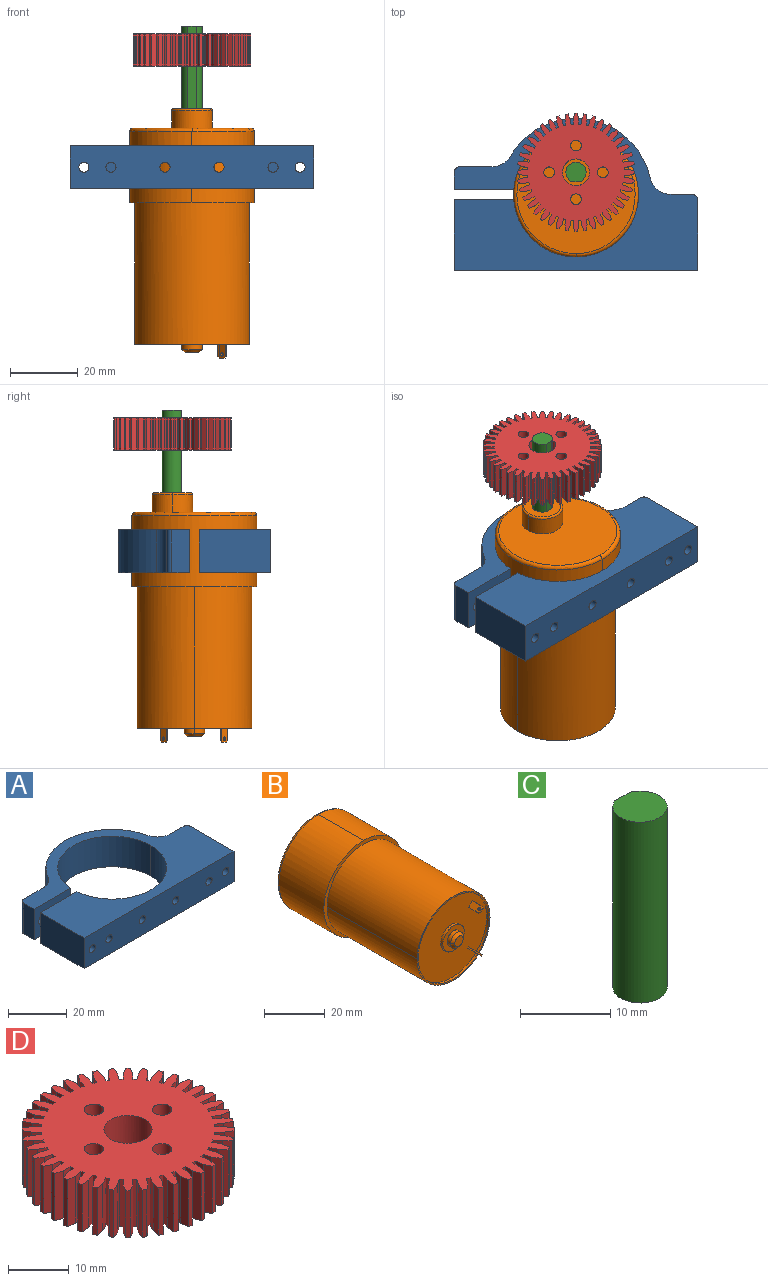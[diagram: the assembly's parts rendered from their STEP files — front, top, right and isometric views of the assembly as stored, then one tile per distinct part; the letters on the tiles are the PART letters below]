
ASSEMBLY  parts=4 mates=3
PART A: 26 faces, bbox 72x45.2x12.7 mm
  f0: cylinder r=1.85mm len=6.7mm, axis (0,-1,0), area 77.9mm2, adj f6,f9
  f1: plane 3.03x3.03mm, normal (0,-1,0), area 7.1mm2, adj f14
  f2: cylinder r=1.5mm len=12.7mm, axis (0,0,-1), area 29.9mm2, adj f12,f17,f18,f19
  f3: cylinder r=6.35mm len=12.7mm, axis (0,0,1), area 108.8mm2, adj f4,f12,f17,f19
  f4: cylinder r=22.5mm len=41.38mm, axis (0,0,1), area 683.2mm2, adj f3,f5,f17,f19
  f5: cylinder r=6.35mm len=12.7mm, axis (0,0,1), area 84mm2, adj f4,f6,f17,f19
  f6: plane 12.7x9.59mm, normal (0,1,0), area 111mm2, adj f0,f5,f7,f17,f19
  f7: cylinder r=1.5mm len=12.7mm, axis (0,0,-1), area 29.9mm2, adj f6,f8,f17,f19
  f8: plane 12.7x5.2mm, normal (-1,0,0), area 66mm2, adj f7,f9,f17,f19
  f9: plane 17.56x12.7mm, normal (0,-1,0), area 212.3mm2, adj f0,f8,f10,f17,f19
  f10: cylinder r=18.5mm len=36.94mm, axis (0,0,1), area 719mm2, adj f9,f11,f17,f19
  f11: cylinder r=18.5mm len=36.94mm, axis (0,0,1), area 702.8mm2, adj f10,f13,f15,f16,f17,f19
  f12: plane 12.7x6.36mm, normal (0,1,0), area 73.7mm2, adj f2,f3,f17,f19,f21
  f13: plane 17.56x12.7mm, normal (0,1,0), area 216mm2, adj f11,f17,f19,f20,f22
  f14: cylinder r=1.5mm len=20mm, axis (0,1,0), area 188.5mm2, adj f1,f24
  f15: cylinder r=1.5mm len=6.63mm, axis (0,1,0), area 58.6mm2, adj f11,f24
  f16: cylinder r=1.5mm len=5.82mm, axis (0,1,0), area 51.8mm2, adj f11,f24
  f17: plane 72x45.23mm, normal (0,0,-1), area 1409.8mm2, adj f2,f3,f4,f5,f6,f7,f8,f9
  f18: plane 21x12.7mm, normal (1,0,0), area 266.7mm2, adj f2,f17,f19,f24
  f19: plane 72x45.23mm, normal (0,0,1), area 1409.8mm2, adj f2,f3,f4,f5,f6,f7,f8,f9
  f20: plane 21x12.7mm, normal (-1,0,0), area 266.7mm2, adj f13,f17,f19,f24
  f21: cylinder r=1.5mm len=22.5mm, axis (0,-1,0), area 212.1mm2, adj f12,f24
  f22: cylinder r=1.5mm len=21mm, axis (0,-1,0), area 197.9mm2, adj f13,f24
  f23: plane 3.03x3.03mm, normal (0,-1,0), area 7.1mm2, adj f25
  f24: plane 72x12.7mm, normal (0,-1,0), area 872mm2, adj f14,f15,f16,f17,f18,f19,f20,f21
  f25: cylinder r=1.5mm len=20mm, axis (0,1,0), area 188.5mm2, adj f23,f24
PART B: 43 faces, bbox 40x73.8x40 mm
  f0: plane 4.02x4mm, normal (0,-1,0), area 12.6mm2, adj f1,f2
  f1: cone r=0mm half-angle=45deg, axis (0,1,0), area 11.1mm2, adj f0,f2,f3
  f2: cone r=0mm half-angle=45deg, axis (0,1,0), area 11.1mm2, adj f0,f1,f4
  f3: cylinder r=3mm len=6mm, axis (0,-1,0), area 14.1mm2, adj f1,f4,f6
  f4: cylinder r=3mm len=6mm, axis (0,-1,0), area 14.1mm2, adj f2,f3,f6
  f5: plane 11.02x11mm, normal (0,1,0), area 95mm2, adj f17,f18
  f6: plane 10.02x10mm, normal (0,-1,0), area 50.3mm2, adj f3,f4,f19,f20
  f7: plane 0.71x0.71mm, normal (-0.5,-0.71,0.5), area 0.4mm2, adj f8,f22,f23,f24
  f8: plane 1.41x1.41mm, normal (0,-1,0), area 0.8mm2, adj f7,f9,f22,f24
  f9: plane 0.71x0.71mm, normal (0.5,-0.71,-0.5), area 0.4mm2, adj f8,f21,f22,f24
  f10: cylinder r=0.5mm len=1.06mm, axis (-0.71,0,-0.71), area 0.8mm2, adj f11,f22,f24
  f11: cylinder r=0.5mm len=1.06mm, axis (-0.71,0,-0.71), area 0.8mm2, adj f10,f22,f24
  f12: plane 1.41x1.41mm, normal (0,-1,0), area 0.8mm2, adj f13,f14,f26,f28
  f13: plane 0.71x0.71mm, normal (0.5,-0.71,0.5), area 0.4mm2, adj f12,f25,f26,f28
  f14: plane 0.71x0.71mm, normal (-0.5,-0.71,-0.5), area 0.4mm2, adj f12,f26,f27,f28
  f15: cylinder r=0.5mm len=1.06mm, axis (-0.71,0,0.71), area 0.8mm2, adj f16,f26,f28
  f16: cylinder r=0.5mm len=1.06mm, axis (-0.71,0,0.71), area 0.8mm2, adj f15,f26,f28
  f17: torus R=5.5mm, axis (0,1,0), area 14.4mm2, adj f5,f18,f29
  f18: torus R=5.5mm, axis (0,1,0), area 14.4mm2, adj f5,f17,f30
  f19: cylinder r=5mm len=10mm, axis (0,-1,0), area 15.7mm2, adj f6,f20,f31
  f20: cylinder r=5mm len=10mm, axis (0,-1,0), area 15.7mm2, adj f6,f19,f31
  f21: plane 4.5x0.35mm, normal (0.71,0,-0.71), area 2.3mm2, adj f9,f22,f24,f31
  f22: plane 5x1.77mm, normal (-0.71,0,-0.71), area 11.5mm2, adj f7,f8,f9,f10,f11,f21,f23,f31
  f23: plane 4.5x0.35mm, normal (-0.71,0,0.71), area 2.3mm2, adj f7,f22,f24,f31
  f24: plane 5x1.77mm, normal (0.71,0,0.71), area 11.5mm2, adj f7,f8,f9,f10,f11,f21,f23,f31
  f25: plane 4.5x0.35mm, normal (0.71,0,0.71), area 2.3mm2, adj f13,f26,f28,f31
  f26: plane 5x1.77mm, normal (0.71,0,-0.71), area 11.5mm2, adj f12,f13,f14,f15,f16,f25,f27,f31
  f27: plane 4.5x0.35mm, normal (-0.71,0,-0.71), area 2.3mm2, adj f14,f26,f28,f31
  f28: plane 5x1.77mm, normal (-0.71,0,0.71), area 11.5mm2, adj f12,f13,f14,f15,f16,f25,f27,f31
  f29: cylinder r=6mm len=12mm, axis (0,1,0), area 99.9mm2, adj f17,f30,f32
  f30: cylinder r=6mm len=12mm, axis (0,1,0), area 99.9mm2, adj f18,f29,f32
  f31: plane 33.04x33mm, normal (0,-1,0), area 774.3mm2, adj f19,f20,f21,f22,f23,f24,f25,f26
  f32: plane 35.07x35mm, normal (0,1,0), area 849mm2, adj f29,f30,f35,f36
  f33: cylinder r=16.5mm len=33mm, axis (0,-1,0), area 51.8mm2, adj f31,f34,f37
  f34: cylinder r=16.5mm len=33mm, axis (0,-1,0), area 51.8mm2, adj f31,f33,f37
  f35: torus R=17.5mm, axis (0,1,0), area 89.5mm2, adj f32,f36,f38
  f36: torus R=17.5mm, axis (0,1,0), area 89.5mm2, adj f32,f35,f39
  f37: plane 34.03x34mm, normal (0,-1,0), area 52.6mm2, adj f33,f34,f40,f41
  f38: cylinder r=18.5mm len=37mm, axis (0,1,0), area 1220.5mm2, adj f35,f39,f42
  f39: cylinder r=18.5mm len=37mm, axis (0,1,0), area 1220.5mm2, adj f36,f38,f42
  f40: cylinder r=17mm len=42mm, axis (0,1,0), area 2243.1mm2, adj f37,f41,f42
  f41: cylinder r=17mm len=42mm, axis (0,1,0), area 2243.1mm2, adj f37,f40,f42
  f42: plane 37.06x37mm, normal (0,-1,0), area 167.3mm2, adj f38,f39,f40,f41
PART C: 4 faces, bbox 6x5.8x24.5 mm
  f0: plane 24.5x2.4mm, normal (0,1,0), area 58.7mm2, adj f1,f2,f3
  f1: cylinder r=3mm len=24.5mm, axis (0,0,-1), area 401.4mm2, adj f0,f2,f3
  f2: plane 6x5.75mm, normal (0,0,1), area 27.9mm2, adj f0,f1
  f3: plane 6x5.75mm, normal (0,0,-1), area 27.9mm2, adj f0,f1
PART D: 257 faces, bbox 34.9x34.9x9.5 mm
  f0: cylinder r=1.59mm len=6.35mm, axis (0,0,1), area 63.3mm2, adj f244,f247,f251
  f1: cylinder r=1.59mm len=6.35mm, axis (0,0,1), area 63.3mm2, adj f244,f248,f252
  f2: cylinder r=1.59mm len=6.35mm, axis (0,0,1), area 63.3mm2, adj f244,f249,f253
  f3: cylinder r=1.59mm len=6.35mm, axis (0,0,1), area 63.3mm2, adj f244,f250,f254
  f4: plane 9.53x1.59mm, normal (-0.97,0.24,0), area 15.6mm2, adj f5,f243,f244,f256
  f5: plane 9.53x1.59mm, normal (-1,0,0), area 15.1mm2, adj f4,f6,f244,f256
  f6: cylinder r=14.29mm len=9.53mm, axis (0,0,1), area 6.2mm2, adj f5,f7,f244,f256
  f7: plane 9.53x1.57mm, normal (0.99,0.16,0), area 15.1mm2, adj f6,f8,f244,f256
  f8: plane 9.53x1.51mm, normal (0.92,0.39,0), area 15.6mm2, adj f7,f9,f244,f256
  f9: plane 9.53x0.78mm, normal (-0.16,0.99,0), area 7.6mm2, adj f8,f10,f244,f256
  f10: plane 9.53x1.63mm, normal (-1,0.09,0), area 15.6mm2, adj f9,f11,f244,f256
  f11: plane 9.53x1.57mm, normal (-0.99,-0.16,0), area 15.1mm2, adj f10,f12,f244,f256
  f12: cylinder r=14.29mm len=9.53mm, axis (0,0,1), area 6.2mm2, adj f11,f13,f244,f256
  f13: plane 9.53x1.51mm, normal (0.95,0.31,0), area 15.1mm2, adj f12,f14,f244,f256
  f14: plane 9.53x1.39mm, normal (0.85,0.53,0), area 15.6mm2, adj f13,f15,f244,f256
  f15: plane 9.53x0.76mm, normal (-0.31,0.95,0), area 7.6mm2, adj f14,f16,f244,f256
  f16: plane 9.53x1.63mm, normal (-1,-0.07,0), area 15.6mm2, adj f15,f17,f244,f256
  f17: plane 9.53x1.51mm, normal (-0.95,-0.31,0), area 15.1mm2, adj f16,f18,f244,f256
  f18: cylinder r=14.29mm len=9.53mm, axis (0,0,1), area 6.2mm2, adj f17,f19,f244,f256
  f19: plane 9.53x1.41mm, normal (0.89,0.45,0), area 15.1mm2, adj f18,f20,f244,f256
  f20: plane 9.53x1.23mm, normal (0.75,0.66,0), area 15.6mm2, adj f19,f21,f244,f256
  f21: plane 9.53x0.71mm, normal (-0.45,0.89,0), area 7.6mm2, adj f20,f22,f244,f256
  f22: plane 9.53x1.59mm, normal (-0.97,-0.22,0), area 15.6mm2, adj f21,f23,f244,f256
  f23: plane 9.53x1.41mm, normal (-0.89,-0.45,0), area 15.1mm2, adj f22,f24,f244,f256
  f24: cylinder r=14.29mm len=9.53mm, axis (0,0,1), area 6.2mm2, adj f23,f25,f244,f256
  f25: plane 9.53x1.28mm, normal (0.81,0.59,0), area 15.1mm2, adj f24,f26,f244,f256
  f26: plane 9.53x1.25mm, normal (0.64,0.77,0), area 15.6mm2, adj f25,f27,f244,f256
  f27: plane 9.53x0.64mm, normal (-0.59,0.81,0), area 7.6mm2, adj f26,f28,f244,f256
  f28: plane 9.53x1.52mm, normal (-0.93,-0.37,0), area 15.6mm2, adj f27,f29,f244,f256
  f29: plane 9.53x1.28mm, normal (-0.81,-0.59,0), area 15.1mm2, adj f28,f30,f244,f256
  f30: cylinder r=14.29mm len=9.53mm, axis (0,0,1), area 6.2mm2, adj f29,f31,f244,f256
  f31: plane 9.53x1.12mm, normal (0.71,0.71,0), area 15.1mm2, adj f30,f32,f244,f256
  f32: plane 9.53x1.4mm, normal (0.51,0.86,0), area 15.6mm2, adj f31,f33,f244,f256
  f33: plane 9.53x0.56mm, normal (-0.71,0.71,0), area 7.6mm2, adj f32,f34,f244,f256
  f34: plane 9.53x1.4mm, normal (-0.86,-0.51,0), area 15.6mm2, adj f33,f35,f244,f256
  f35: plane 9.53x1.12mm, normal (-0.71,-0.71,0), area 15.1mm2, adj f34,f36,f244,f256
  f36: cylinder r=14.29mm len=9.53mm, axis (0,0,1), area 6.2mm2, adj f35,f37,f244,f256
  f37: plane 9.53x1.28mm, normal (0.59,0.81,0), area 15.1mm2, adj f36,f38,f244,f256
  f38: plane 9.53x1.52mm, normal (0.37,0.93,0), area 15.6mm2, adj f37,f39,f244,f256
  f39: plane 9.53x0.64mm, normal (-0.81,0.59,0), area 7.6mm2, adj f38,f40,f244,f256
  f40: plane 9.53x1.25mm, normal (-0.77,-0.64,0), area 15.6mm2, adj f39,f41,f244,f256
  f41: plane 9.53x1.28mm, normal (-0.59,-0.81,0), area 15.1mm2, adj f40,f42,f244,f256
  f42: cylinder r=14.29mm len=9.53mm, axis (0,0,1), area 6.2mm2, adj f41,f43,f244,f256
  f43: plane 9.53x1.41mm, normal (0.45,0.89,0), area 15.1mm2, adj f42,f44,f244,f256
  f44: plane 9.53x1.59mm, normal (0.22,0.97,0), area 15.6mm2, adj f43,f45,f244,f256
  f45: plane 9.53x0.71mm, normal (-0.89,0.45,0), area 7.6mm2, adj f44,f46,f244,f256
  f46: plane 9.53x1.23mm, normal (-0.66,-0.75,0), area 15.6mm2, adj f45,f47,f244,f256
  f47: plane 9.53x1.41mm, normal (-0.45,-0.89,0), area 15.1mm2, adj f46,f48,f244,f256
  f48: cylinder r=14.29mm len=9.53mm, axis (0,0,1), area 6.2mm2, adj f47,f49,f244,f256
  f49: plane 9.53x1.51mm, normal (0.31,0.95,0), area 15.1mm2, adj f48,f50,f244,f256
  f50: plane 9.53x1.63mm, normal (0.07,1,0), area 15.6mm2, adj f49,f51,f244,f256
  f51: plane 9.53x0.76mm, normal (-0.95,0.31,0), area 7.6mm2, adj f50,f52,f244,f256
  f52: plane 9.53x1.39mm, normal (-0.53,-0.85,0), area 15.6mm2, adj f51,f53,f244,f256
  f53: plane 9.53x1.51mm, normal (-0.31,-0.95,0), area 15.1mm2, adj f52,f54,f244,f256
  f54: cylinder r=14.29mm len=9.53mm, axis (0,0,1), area 6.2mm2, adj f53,f55,f244,f256
  f55: plane 9.53x1.57mm, normal (0.16,0.99,0), area 15.1mm2, adj f54,f56,f244,f256
  f56: plane 9.53x1.63mm, normal (-0.09,1,0), area 15.6mm2, adj f55,f57,f244,f256
  f57: plane 9.53x0.78mm, normal (-0.99,0.16,0), area 7.6mm2, adj f56,f58,f244,f256
  f58: plane 9.53x1.51mm, normal (-0.39,-0.92,0), area 15.6mm2, adj f57,f59,f244,f256
  f59: plane 9.53x1.57mm, normal (-0.16,-0.99,0), area 15.1mm2, adj f58,f60,f244,f256
  f60: cylinder r=14.29mm len=9.53mm, axis (0,0,1), area 6.2mm2, adj f59,f61,f244,f256
  f61: plane 9.53x1.59mm, normal (0,1,0), area 15.1mm2, adj f60,f62,f244,f256
  f62: plane 9.53x1.59mm, normal (-0.24,0.97,0), area 15.6mm2, adj f61,f63,f244,f256
  f63: plane 9.53x0.79mm, normal (-1,0,0), area 7.6mm2, adj f62,f64,f244,f256
  f64: plane 9.53x1.59mm, normal (-0.24,-0.97,0), area 15.6mm2, adj f63,f65,f244,f256
  f65: plane 9.53x1.59mm, normal (0,-1,0), area 15.1mm2, adj f64,f66,f244,f256
  f66: cylinder r=14.29mm len=9.53mm, axis (0,0,1), area 6.2mm2, adj f65,f67,f244,f256
  f67: plane 9.53x1.57mm, normal (-0.16,0.99,0), area 15.1mm2, adj f66,f68,f244,f256
  f68: plane 9.53x1.51mm, normal (-0.39,0.92,0), area 15.6mm2, adj f67,f69,f244,f256
  f69: plane 9.53x0.78mm, normal (-0.99,-0.16,0), area 7.6mm2, adj f68,f70,f244,f256
  f70: plane 9.53x1.63mm, normal (-0.09,-1,0), area 15.6mm2, adj f69,f71,f244,f256
  f71: plane 9.53x1.57mm, normal (0.16,-0.99,0), area 15.1mm2, adj f70,f72,f244,f256
  f72: cylinder r=14.29mm len=9.53mm, axis (0,0,1), area 6.2mm2, adj f71,f73,f244,f256
  f73: plane 9.53x1.51mm, normal (-0.31,0.95,0), area 15.1mm2, adj f72,f74,f244,f256
  f74: plane 9.53x1.39mm, normal (-0.53,0.85,0), area 15.6mm2, adj f73,f75,f244,f256
  f75: plane 9.53x0.76mm, normal (-0.95,-0.31,0), area 7.6mm2, adj f74,f76,f244,f256
  f76: plane 9.53x1.63mm, normal (0.07,-1,0), area 15.6mm2, adj f75,f77,f244,f256
  f77: plane 9.53x1.51mm, normal (0.31,-0.95,0), area 15.1mm2, adj f76,f78,f244,f256
  f78: cylinder r=14.29mm len=9.53mm, axis (0,0,1), area 6.2mm2, adj f77,f79,f244,f256
  f79: plane 9.53x1.41mm, normal (-0.45,0.89,0), area 15.1mm2, adj f78,f80,f244,f256
  f80: plane 9.53x1.23mm, normal (-0.66,0.75,0), area 15.6mm2, adj f79,f81,f244,f256
  f81: plane 9.53x0.71mm, normal (-0.89,-0.45,0), area 7.6mm2, adj f80,f82,f244,f256
  f82: plane 9.53x1.59mm, normal (0.22,-0.97,0), area 15.6mm2, adj f81,f83,f244,f256
  f83: plane 9.53x1.41mm, normal (0.45,-0.89,0), area 15.1mm2, adj f82,f84,f244,f256
  f84: cylinder r=14.29mm len=9.53mm, axis (0,0,1), area 6.2mm2, adj f83,f85,f244,f256
  f85: plane 9.53x1.28mm, normal (-0.59,0.81,0), area 15.1mm2, adj f84,f86,f244,f256
  f86: plane 9.53x1.25mm, normal (-0.77,0.64,0), area 15.6mm2, adj f85,f87,f244,f256
  f87: plane 9.53x0.64mm, normal (-0.81,-0.59,0), area 7.6mm2, adj f86,f88,f244,f256
  f88: plane 9.53x1.52mm, normal (0.37,-0.93,0), area 15.6mm2, adj f87,f89,f244,f256
  f89: plane 9.53x1.28mm, normal (0.59,-0.81,0), area 15.1mm2, adj f88,f90,f244,f256
  f90: cylinder r=14.29mm len=9.53mm, axis (0,0,1), area 6.2mm2, adj f89,f91,f244,f256
  f91: plane 9.53x1.12mm, normal (-0.71,0.71,0), area 15.1mm2, adj f90,f92,f244,f256
  f92: plane 9.53x1.4mm, normal (-0.86,0.51,0), area 15.6mm2, adj f91,f93,f244,f256
  f93: plane 9.53x0.56mm, normal (-0.71,-0.71,0), area 7.6mm2, adj f92,f94,f244,f256
  f94: plane 9.53x1.4mm, normal (0.51,-0.86,0), area 15.6mm2, adj f93,f95,f244,f256
  f95: plane 9.53x1.12mm, normal (0.71,-0.71,0), area 15.1mm2, adj f94,f96,f244,f256
  f96: cylinder r=14.29mm len=9.53mm, axis (0,0,1), area 6.2mm2, adj f95,f97,f244,f256
  f97: plane 9.53x1.28mm, normal (-0.81,0.59,0), area 15.1mm2, adj f96,f98,f244,f256
  f98: plane 9.53x1.52mm, normal (-0.93,0.37,0), area 15.6mm2, adj f97,f99,f244,f256
  f99: plane 9.53x0.64mm, normal (-0.59,-0.81,0), area 7.6mm2, adj f98,f100,f244,f256
  f100: plane 9.53x1.25mm, normal (0.64,-0.77,0), area 15.6mm2, adj f99,f101,f244,f256
  f101: plane 9.53x1.28mm, normal (0.81,-0.59,0), area 15.1mm2, adj f100,f102,f244,f256
  f102: cylinder r=14.29mm len=9.53mm, axis (0,0,1), area 6.2mm2, adj f101,f103,f244,f256
  f103: plane 9.53x1.41mm, normal (-0.89,0.45,0), area 15.1mm2, adj f102,f104,f244,f256
  f104: plane 9.53x1.59mm, normal (-0.97,0.22,0), area 15.6mm2, adj f103,f105,f244,f256
  f105: plane 9.53x0.71mm, normal (-0.45,-0.89,0), area 7.6mm2, adj f104,f106,f244,f256
  f106: plane 9.53x1.23mm, normal (0.75,-0.66,0), area 15.6mm2, adj f105,f107,f244,f256
  f107: plane 9.53x1.41mm, normal (0.89,-0.45,0), area 15.1mm2, adj f106,f108,f244,f256
  f108: cylinder r=14.29mm len=9.53mm, axis (0,0,1), area 6.2mm2, adj f107,f109,f244,f256
  f109: plane 9.53x1.51mm, normal (-0.95,0.31,0), area 15.1mm2, adj f108,f110,f244,f256
  f110: plane 9.53x1.63mm, normal (-1,0.07,0), area 15.6mm2, adj f109,f111,f244,f256
  f111: plane 9.53x0.76mm, normal (-0.31,-0.95,0), area 7.6mm2, adj f110,f112,f244,f256
  f112: plane 9.53x1.39mm, normal (0.85,-0.53,0), area 15.6mm2, adj f111,f113,f244,f256
  f113: plane 9.53x1.51mm, normal (0.95,-0.31,0), area 15.1mm2, adj f112,f114,f244,f256
  f114: cylinder r=14.29mm len=9.53mm, axis (0,0,1), area 6.2mm2, adj f113,f115,f244,f256
  f115: plane 9.53x1.57mm, normal (-0.99,0.16,0), area 15.1mm2, adj f114,f116,f244,f256
  f116: plane 9.53x1.63mm, normal (-1,-0.09,0), area 15.6mm2, adj f115,f117,f244,f256
  f117: plane 9.53x0.78mm, normal (-0.16,-0.99,0), area 7.6mm2, adj f116,f118,f244,f256
  f118: plane 9.53x1.51mm, normal (0.92,-0.39,0), area 15.6mm2, adj f117,f119,f244,f256
  f119: plane 9.53x1.57mm, normal (0.99,-0.16,0), area 15.1mm2, adj f118,f120,f244,f256
  f120: cylinder r=14.29mm len=9.53mm, axis (0,0,1), area 6.2mm2, adj f119,f121,f244,f256
  f121: plane 9.53x1.59mm, normal (-1,0,0), area 15.1mm2, adj f120,f122,f244,f256
  f122: plane 9.53x1.59mm, normal (-0.97,-0.24,0), area 15.6mm2, adj f121,f123,f244,f256
  f123: plane 9.53x0.79mm, normal (0,-1,0), area 7.6mm2, adj f122,f124,f244,f256
  f124: plane 9.53x1.59mm, normal (0.97,-0.24,0), area 15.6mm2, adj f123,f125,f244,f256
  f125: plane 9.53x1.59mm, normal (1,0,0), area 15.1mm2, adj f124,f126,f244,f256
  f126: cylinder r=14.29mm len=9.53mm, axis (0,0,1), area 6.2mm2, adj f125,f127,f244,f256
  f127: plane 9.53x1.57mm, normal (-0.99,-0.16,0), area 15.1mm2, adj f126,f128,f244,f256
  f128: plane 9.53x1.51mm, normal (-0.92,-0.39,0), area 15.6mm2, adj f127,f129,f244,f256
  f129: plane 9.53x0.78mm, normal (0.16,-0.99,0), area 7.6mm2, adj f128,f130,f244,f256
  f130: plane 9.53x1.63mm, normal (1,-0.09,0), area 15.6mm2, adj f129,f131,f244,f256
  f131: plane 9.53x1.57mm, normal (0.99,0.16,0), area 15.1mm2, adj f130,f132,f244,f256
  f132: cylinder r=14.29mm len=9.53mm, axis (0,0,1), area 6.2mm2, adj f131,f133,f244,f256
  f133: plane 9.53x1.51mm, normal (-0.95,-0.31,0), area 15.1mm2, adj f132,f134,f244,f256
  f134: plane 9.53x1.39mm, normal (-0.85,-0.53,0), area 15.6mm2, adj f133,f135,f244,f256
  f135: plane 9.53x0.76mm, normal (0.31,-0.95,0), area 7.6mm2, adj f134,f136,f244,f256
  f136: plane 9.53x1.63mm, normal (1,0.07,0), area 15.6mm2, adj f135,f137,f244,f256
  f137: plane 9.53x1.51mm, normal (0.95,0.31,0), area 15.1mm2, adj f136,f138,f244,f256
  f138: cylinder r=14.29mm len=9.53mm, axis (0,0,1), area 6.2mm2, adj f137,f139,f244,f256
  f139: plane 9.53x1.41mm, normal (-0.89,-0.45,0), area 15.1mm2, adj f138,f140,f244,f256
  f140: plane 9.53x1.23mm, normal (-0.75,-0.66,0), area 15.6mm2, adj f139,f141,f244,f256
  f141: plane 9.53x0.71mm, normal (0.45,-0.89,0), area 7.6mm2, adj f140,f142,f244,f256
  f142: plane 9.53x1.59mm, normal (0.97,0.22,0), area 15.6mm2, adj f141,f143,f244,f256
  f143: plane 9.53x1.41mm, normal (0.89,0.45,0), area 15.1mm2, adj f142,f144,f244,f256
  f144: cylinder r=14.29mm len=9.53mm, axis (0,0,1), area 6.2mm2, adj f143,f145,f244,f256
  f145: plane 9.53x1.28mm, normal (-0.81,-0.59,0), area 15.1mm2, adj f144,f146,f244,f256
  f146: plane 9.53x1.25mm, normal (-0.64,-0.77,0), area 15.6mm2, adj f145,f147,f244,f256
  f147: plane 9.53x0.64mm, normal (0.59,-0.81,0), area 7.6mm2, adj f146,f148,f244,f256
  f148: plane 9.53x1.52mm, normal (0.93,0.37,0), area 15.6mm2, adj f147,f149,f244,f256
  f149: plane 9.53x1.28mm, normal (0.81,0.59,0), area 15.1mm2, adj f148,f150,f244,f256
  f150: cylinder r=14.29mm len=9.53mm, axis (0,0,1), area 6.2mm2, adj f149,f151,f244,f256
  f151: plane 9.53x1.12mm, normal (-0.71,-0.71,0), area 15.1mm2, adj f150,f152,f244,f256
  f152: plane 9.53x1.4mm, normal (-0.51,-0.86,0), area 15.6mm2, adj f151,f153,f244,f256
  f153: plane 9.53x0.56mm, normal (0.71,-0.71,0), area 7.6mm2, adj f152,f154,f244,f256
  f154: plane 9.53x1.4mm, normal (0.86,0.51,0), area 15.6mm2, adj f153,f155,f244,f256
  f155: plane 9.53x1.12mm, normal (0.71,0.71,0), area 15.1mm2, adj f154,f156,f244,f256
  f156: cylinder r=14.29mm len=9.53mm, axis (0,0,1), area 6.2mm2, adj f155,f157,f244,f256
  f157: plane 9.53x1.28mm, normal (-0.59,-0.81,0), area 15.1mm2, adj f156,f158,f244,f256
  f158: plane 9.53x1.52mm, normal (-0.37,-0.93,0), area 15.6mm2, adj f157,f159,f244,f256
  f159: plane 9.53x0.64mm, normal (0.81,-0.59,0), area 7.6mm2, adj f158,f160,f244,f256
  f160: plane 9.53x1.25mm, normal (0.77,0.64,0), area 15.6mm2, adj f159,f161,f244,f256
  f161: plane 9.53x1.28mm, normal (0.59,0.81,0), area 15.1mm2, adj f160,f162,f244,f256
  f162: cylinder r=14.29mm len=9.53mm, axis (0,0,1), area 6.2mm2, adj f161,f163,f244,f256
  f163: plane 9.53x1.41mm, normal (-0.45,-0.89,0), area 15.1mm2, adj f162,f164,f244,f256
  f164: plane 9.53x1.59mm, normal (-0.22,-0.97,0), area 15.6mm2, adj f163,f165,f244,f256
  f165: plane 9.53x0.71mm, normal (0.89,-0.45,0), area 7.6mm2, adj f164,f166,f244,f256
  f166: plane 9.53x1.23mm, normal (0.66,0.75,0), area 15.6mm2, adj f165,f167,f244,f256
  f167: plane 9.53x1.41mm, normal (0.45,0.89,0), area 15.1mm2, adj f166,f168,f244,f256
  f168: cylinder r=14.29mm len=9.53mm, axis (0,0,1), area 6.2mm2, adj f167,f169,f244,f256
  f169: plane 9.53x1.51mm, normal (-0.31,-0.95,0), area 15.1mm2, adj f168,f170,f244,f256
  f170: plane 9.53x1.63mm, normal (-0.07,-1,0), area 15.6mm2, adj f169,f171,f244,f256
  f171: plane 9.53x0.76mm, normal (0.95,-0.31,0), area 7.6mm2, adj f170,f172,f244,f256
  f172: plane 9.53x1.39mm, normal (0.53,0.85,0), area 15.6mm2, adj f171,f173,f244,f256
  f173: plane 9.53x1.51mm, normal (0.31,0.95,0), area 15.1mm2, adj f172,f174,f244,f256
  f174: cylinder r=14.29mm len=9.53mm, axis (0,0,1), area 6.2mm2, adj f173,f175,f244,f256
  f175: plane 9.53x1.57mm, normal (-0.16,-0.99,0), area 15.1mm2, adj f174,f176,f244,f256
  f176: plane 9.53x1.63mm, normal (0.09,-1,0), area 15.6mm2, adj f175,f177,f244,f256
  f177: plane 9.53x0.78mm, normal (0.99,-0.16,0), area 7.6mm2, adj f176,f178,f244,f256
  f178: plane 9.53x1.51mm, normal (0.39,0.92,0), area 15.6mm2, adj f177,f179,f244,f256
  f179: plane 9.53x1.57mm, normal (0.16,0.99,0), area 15.1mm2, adj f178,f180,f244,f256
  f180: cylinder r=14.29mm len=9.53mm, axis (0,0,1), area 6.2mm2, adj f179,f181,f244,f256
  f181: plane 9.53x1.59mm, normal (0,-1,0), area 15.1mm2, adj f180,f182,f244,f256
  f182: plane 9.53x1.59mm, normal (0.24,-0.97,0), area 15.6mm2, adj f181,f183,f244,f256
  f183: plane 9.53x0.79mm, normal (1,0,0), area 7.6mm2, adj f182,f184,f244,f256
  f184: plane 9.53x1.59mm, normal (0.24,0.97,0), area 15.6mm2, adj f183,f185,f244,f256
  f185: plane 9.53x1.59mm, normal (0,1,0), area 15.1mm2, adj f184,f186,f244,f256
  f186: cylinder r=14.29mm len=9.53mm, axis (0,0,1), area 6.2mm2, adj f185,f187,f244,f256
  f187: plane 9.53x1.57mm, normal (0.16,-0.99,0), area 15.1mm2, adj f186,f188,f244,f256
  f188: plane 9.53x1.51mm, normal (0.39,-0.92,0), area 15.6mm2, adj f187,f189,f244,f256
  f189: plane 9.53x0.78mm, normal (0.99,0.16,0), area 7.6mm2, adj f188,f190,f244,f256
  f190: plane 9.53x1.63mm, normal (0.09,1,0), area 15.6mm2, adj f189,f191,f244,f256
  f191: plane 9.53x1.57mm, normal (-0.16,0.99,0), area 15.1mm2, adj f190,f192,f244,f256
  f192: cylinder r=14.29mm len=9.53mm, axis (0,0,1), area 6.2mm2, adj f191,f193,f244,f256
  f193: plane 9.53x1.51mm, normal (0.31,-0.95,0), area 15.1mm2, adj f192,f194,f244,f256
  f194: plane 9.53x1.39mm, normal (0.53,-0.85,0), area 15.6mm2, adj f193,f195,f244,f256
  f195: plane 9.53x0.76mm, normal (0.95,0.31,0), area 7.6mm2, adj f194,f196,f244,f256
  f196: plane 9.53x1.63mm, normal (-0.07,1,0), area 15.6mm2, adj f195,f197,f244,f256
  f197: plane 9.53x1.51mm, normal (-0.31,0.95,0), area 15.1mm2, adj f196,f198,f244,f256
  f198: cylinder r=14.29mm len=9.53mm, axis (0,0,1), area 6.2mm2, adj f197,f199,f244,f256
  f199: plane 9.53x1.41mm, normal (0.45,-0.89,0), area 15.1mm2, adj f198,f200,f244,f256
  f200: plane 9.53x1.23mm, normal (0.66,-0.75,0), area 15.6mm2, adj f199,f201,f244,f256
  f201: plane 9.53x0.71mm, normal (0.89,0.45,0), area 7.6mm2, adj f200,f202,f244,f256
  f202: plane 9.53x1.59mm, normal (-0.22,0.97,0), area 15.6mm2, adj f201,f203,f244,f256
  f203: plane 9.53x1.41mm, normal (-0.45,0.89,0), area 15.1mm2, adj f202,f204,f244,f256
  f204: cylinder r=14.29mm len=9.53mm, axis (0,0,1), area 6.2mm2, adj f203,f205,f244,f256
  f205: plane 9.53x1.28mm, normal (0.59,-0.81,0), area 15.1mm2, adj f204,f206,f244,f256
  f206: plane 9.53x1.25mm, normal (0.77,-0.64,0), area 15.6mm2, adj f205,f207,f244,f256
  f207: plane 9.53x0.64mm, normal (0.81,0.59,0), area 7.6mm2, adj f206,f208,f244,f256
  f208: plane 9.53x1.52mm, normal (-0.37,0.93,0), area 15.6mm2, adj f207,f209,f244,f256
  f209: plane 9.53x1.28mm, normal (-0.59,0.81,0), area 15.1mm2, adj f208,f210,f244,f256
  f210: cylinder r=14.29mm len=9.53mm, axis (0,0,1), area 6.2mm2, adj f209,f211,f244,f256
  f211: plane 9.53x1.12mm, normal (0.71,-0.71,0), area 15.1mm2, adj f210,f212,f244,f256
  f212: plane 9.53x1.4mm, normal (0.86,-0.51,0), area 15.6mm2, adj f211,f213,f244,f256
  f213: plane 9.53x0.56mm, normal (0.71,0.71,0), area 7.6mm2, adj f212,f214,f244,f256
  f214: plane 9.53x1.4mm, normal (-0.51,0.86,0), area 15.6mm2, adj f213,f215,f244,f256
  f215: plane 9.53x1.12mm, normal (-0.71,0.71,0), area 15.1mm2, adj f214,f216,f244,f256
  f216: cylinder r=14.29mm len=9.53mm, axis (0,0,1), area 6.2mm2, adj f215,f217,f244,f256
  f217: plane 9.53x1.28mm, normal (0.81,-0.59,0), area 15.1mm2, adj f216,f218,f244,f256
  f218: plane 9.53x1.52mm, normal (0.93,-0.37,0), area 15.6mm2, adj f217,f219,f244,f256
  f219: plane 9.53x0.64mm, normal (0.59,0.81,0), area 7.6mm2, adj f218,f220,f244,f256
  f220: plane 9.53x1.25mm, normal (-0.64,0.77,0), area 15.6mm2, adj f219,f221,f244,f256
  f221: plane 9.53x1.28mm, normal (-0.81,0.59,0), area 15.1mm2, adj f220,f222,f244,f256
  f222: cylinder r=14.29mm len=9.53mm, axis (0,0,1), area 6.2mm2, adj f221,f223,f244,f256
  f223: plane 9.53x1.41mm, normal (0.89,-0.45,0), area 15.1mm2, adj f222,f224,f244,f256
  f224: plane 9.53x1.59mm, normal (0.97,-0.22,0), area 15.6mm2, adj f223,f225,f244,f256
  f225: plane 9.53x0.71mm, normal (0.45,0.89,0), area 7.6mm2, adj f224,f226,f244,f256
  f226: plane 9.53x1.23mm, normal (-0.75,0.66,0), area 15.6mm2, adj f225,f227,f244,f256
  f227: plane 9.53x1.41mm, normal (-0.89,0.45,0), area 15.1mm2, adj f226,f228,f244,f256
  f228: cylinder r=14.29mm len=9.53mm, axis (0,0,1), area 6.2mm2, adj f227,f229,f244,f256
  f229: plane 9.53x1.51mm, normal (0.95,-0.31,0), area 15.1mm2, adj f228,f230,f244,f256
  f230: plane 9.53x1.63mm, normal (1,-0.07,0), area 15.6mm2, adj f229,f231,f244,f256
  f231: plane 9.53x0.76mm, normal (0.31,0.95,0), area 7.6mm2, adj f230,f232,f244,f256
  f232: plane 9.53x1.39mm, normal (-0.85,0.53,0), area 15.6mm2, adj f231,f233,f244,f256
  f233: plane 9.53x1.51mm, normal (-0.95,0.31,0), area 15.1mm2, adj f232,f234,f244,f256
  f234: cylinder r=14.29mm len=9.53mm, axis (0,0,1), area 6.2mm2, adj f233,f235,f244,f256
  f235: plane 9.53x1.57mm, normal (0.99,-0.16,0), area 15.1mm2, adj f234,f236,f244,f256
  f236: plane 9.53x1.63mm, normal (1,0.09,0), area 15.6mm2, adj f235,f237,f244,f256
  f237: plane 9.53x0.78mm, normal (0.16,0.99,0), area 7.6mm2, adj f236,f238,f244,f256
  f238: plane 9.53x1.51mm, normal (-0.92,0.39,0), area 15.6mm2, adj f237,f239,f244,f256
  f239: plane 9.53x1.57mm, normal (-0.99,0.16,0), area 15.1mm2, adj f238,f240,f244,f256
  f240: cylinder r=14.29mm len=9.53mm, axis (0,0,1), area 6.2mm2, adj f239,f241,f244,f256
  f241: plane 9.53x1.59mm, normal (1,0,0), area 15.1mm2, adj f240,f242,f244,f256
  f242: plane 9.53x1.59mm, normal (0.97,0.24,0), area 15.6mm2, adj f241,f243,f244,f256
  f243: plane 9.53x0.79mm, normal (0,1,0), area 7.6mm2, adj f4,f242,f244,f256
  f244: plane 34.88x34.88mm, normal (0,0,1), area 735.6mm2, adj f0,f1,f2,f3,f4,f5,f6,f7
  f245: cylinder r=3.97mm len=7.94mm, axis (0,0,1), area 158.3mm2, adj f244,f246,f255
  f246: extruded ~7.94x3.97mm, area 39.6mm2, adj f245,f255,f256
  f247: extruded ~3.18x3.18mm, area 15.8mm2, adj f0,f251,f256
  f248: extruded ~3.18x3.18mm, area 15.8mm2, adj f1,f252,f256
  f249: extruded ~3.18x3.18mm, area 15.8mm2, adj f2,f253,f256
  f250: extruded ~3.18x3.18mm, area 15.8mm2, adj f3,f254,f256
  f251: extruded ~3.18x3.18mm, area 15.8mm2, adj f0,f247,f256
  f252: extruded ~3.18x3.18mm, area 15.8mm2, adj f1,f248,f256
  f253: extruded ~3.18x3.18mm, area 15.8mm2, adj f2,f249,f256
  f254: extruded ~3.18x3.18mm, area 15.8mm2, adj f3,f250,f256
  f255: extruded ~7.94x3.97mm, area 39.6mm2, adj f245,f246,f256
  f256: plane 34.88x34.88mm, normal (0,0,-1), area 735.6mm2, adj f4,f5,f6,f7,f8,f9,f10,f11
PLACE A t=(16.94,12.69,1.94)mm
PLACE B rot(axis=(1,0,0),90deg) t=(16.94,12.69,-8.56)mm
PLACE C rot(axis=(1,0,0),180deg) t=(16.94,19.19,43.74)mm
PLACE D t=(16.94,19.19,35.03)mm
MATE revolute C.f1 <-> B.f17  axis (0,0,-1) through (16.94,19.19,19.24)mm
MATE cylindrical B.f1 <-> A.f4  axis (0,0,1) through (16.94,12.69,1.94)mm
MATE cylindrical D.f6 <-> C.f1  axis (0,0,1) through (16.94,19.19,38.2)mm
